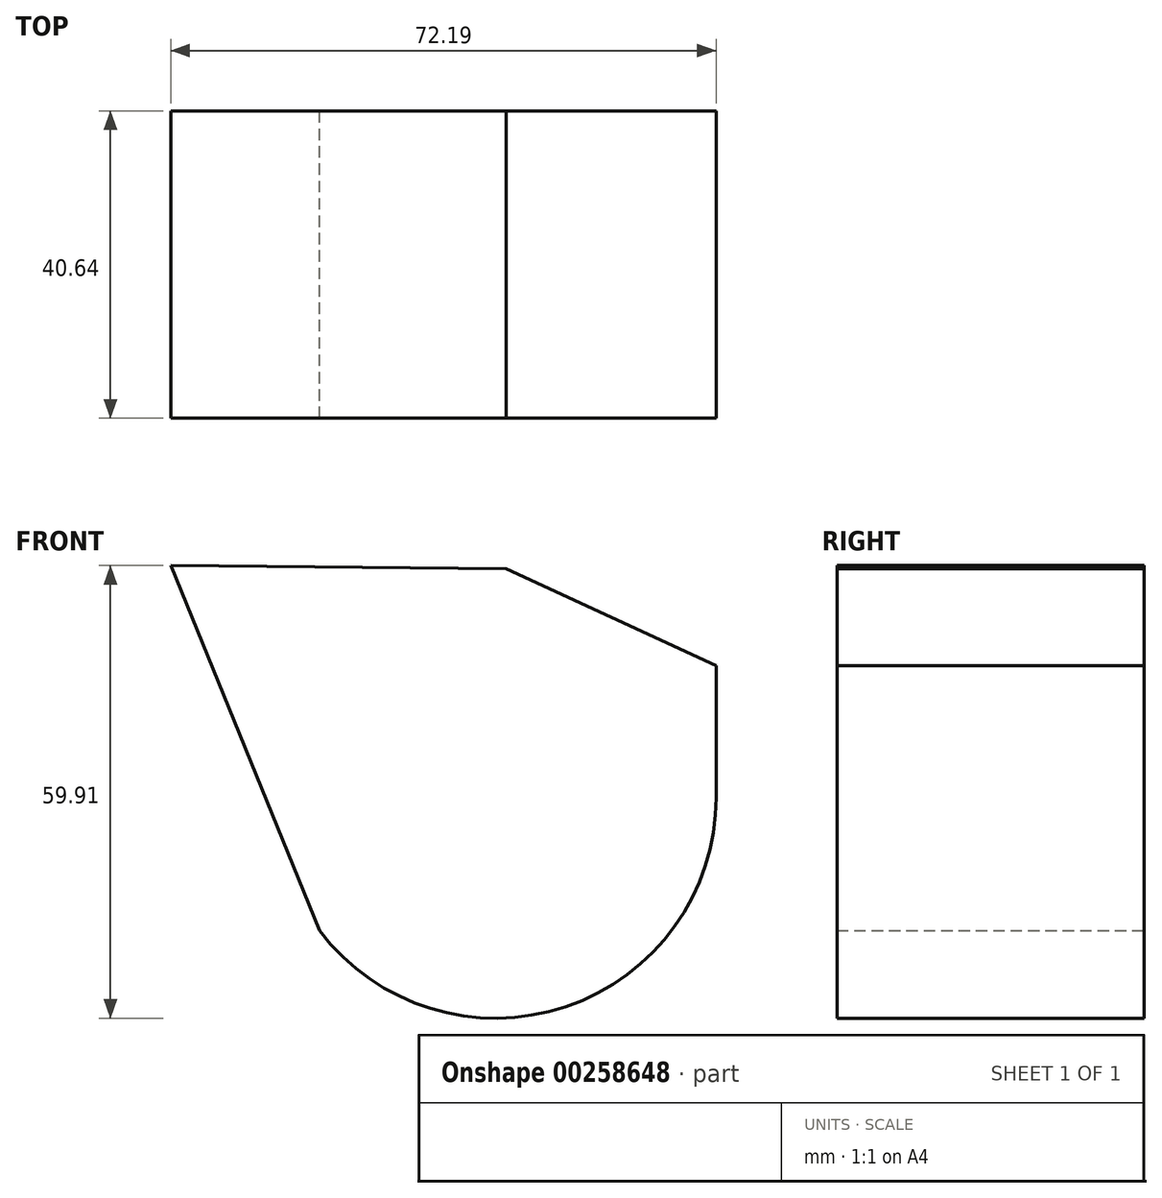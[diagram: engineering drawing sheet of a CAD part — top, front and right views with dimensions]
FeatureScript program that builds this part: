
annotation { "Feature Type Name" : "Feature", "Feature Type Description" : "" }
export const myFeature = defineFeature(function(context is Context, id is Id, definition is map)
    precondition{}
    {
        {
            var Q0;
            Q0=qCreatedBy(makeId("Front.planeOp"),FACE);
            var sketch = newSketch(context, id + "F0", { "sketchPlane" : qUnion([Q0])});
            skLineSegment(sketch, "E0", {"start": v(11.2, 47.92) * mm, "end": v(39, 35.06) * mm});
            skLineSegment(sketch, "E1", {"start": v(39, 35.06) * mm, "end": v(39, 17.63) * mm});
            skArc(sketch, "E2", {"start": v(-13.48, 0) * mm, "mid": v(19.1, -10.05) * mm, "end": v(39, 17.63) * mm});
            skLineSegment(sketch, "E3", {"start": v(-13.48, 0) * mm, "end": v(-33.2, 48.34) * mm});
            skLineSegment(sketch, "E4", {"start": v(-33.2, 48.34) * mm, "end": v(11.2, 47.92) * mm});
            skSolve(sketch);
        }
        {
            var Q0;
            Q0=makeQuery(id+"F0.imprint","IMPRINT",FACE,{"disambiguationData":[TD([[makeQuery(id+"F0.imprint","IMPRINT",EDGE,{"derivedFrom":sQuery(id+"F0.wireOp",EDGE,"E0")}),-1.0]])]});
            var Q1;
            Q1 = qSketchRegion(id + "F0", true);
            extrude(context, id + "F1", {"entities" : qUnion([Q0, Q1]), "depth" : 40.64 * mm});
        }
    });
